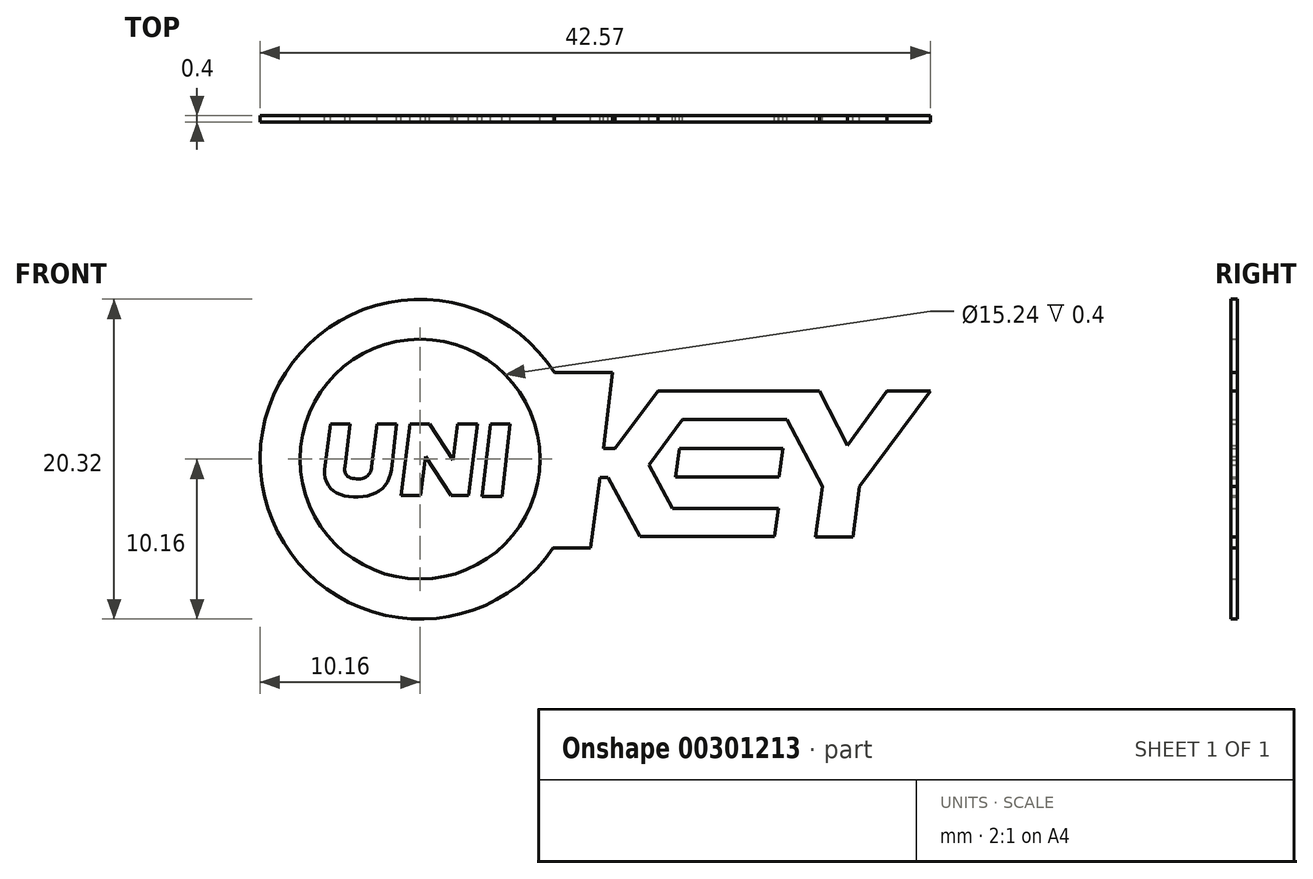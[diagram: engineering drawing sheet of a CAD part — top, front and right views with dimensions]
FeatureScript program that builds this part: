
annotation { "Feature Type Name" : "Feature", "Feature Type Description" : "" }
export const myFeature = defineFeature(function(context is Context, id is Id, definition is map)
    precondition{}
    {
        {
            var Q0;
            Q0=qCreatedBy(makeId("Front.planeOp"),FACE);
            var sketch = newSketch(context, id + "F0", { "sketchPlane" : qUnion([Q0])});
            skSolve(sketch);
        }
        {
            var Q0;
            Q0=qCreatedBy(makeId("Front.planeOp"),FACE);
            var sketch = newSketch(context, id + "F1", { "sketchPlane" : qUnion([Q0])});
            skLineSegment(sketch, "E0.0", {"start": v(106.6, 50.8) * mm, "end": v(0, 50.8) * mm});
            skPoint(sketch, "E1.0", {"position": v(0, 25.4) * mm});
            skLineSegment(sketch, "E2.0", {"start": v(0, 0) * mm, "end": v(106.6, 0) * mm});
            skCircle(sketch, "E3", {"center": v(25.4, 25.4) * mm, "radius": 25.4 * mm});
            skPoint(sketch, "E3.second.point", {"position": v(25.4, 50.8) * mm});
            skPoint(sketch, "E3.third.point", {"position": v(25.4, 0) * mm});
            skCircle(sketch, "E4", {"center": v(25.4, 25.4) * mm, "radius": 19.05 * mm});
            skLineSegment(sketch, "E5", {"start": v(46.75, 39.16) * mm, "end": v(55.96, 39.16) * mm});
            skLineSegment(sketch, "E6", {"start": v(55.96, 39.16) * mm, "end": v(54.52, 27.13) * mm});
            skLineSegment(sketch, "E7", {"start": v(63.19, 36.2) * mm, "end": v(88.82, 36.2) * mm});
            skLineSegment(sketch, "E8", {"start": v(88.82, 36.2) * mm, "end": v(93.23, 27.6) * mm});
            skLineSegment(sketch, "E9", {"start": v(93.23, 27.6) * mm, "end": v(99.5, 36.2) * mm});
            skLineSegment(sketch, "E10", {"start": v(99.5, 36.2) * mm, "end": v(106.42, 36.2) * mm});
            skLineSegment(sketch, "E11", {"start": v(106.42, 36.2) * mm, "end": v(95.19, 21.06) * mm});
            skLineSegment(sketch, "E12", {"start": v(95.19, 21.06) * mm, "end": v(94.13, 13.05) * mm});
            skLineSegment(sketch, "E13", {"start": v(94.13, 13.05) * mm, "end": v(88.2, 13.05) * mm});
            skLineSegment(sketch, "E14", {"start": v(88.2, 13.05) * mm, "end": v(89.26, 21.06) * mm});
            skLineSegment(sketch, "E15", {"start": v(89.26, 21.06) * mm, "end": v(83.67, 31.67) * mm});
            skLineSegment(sketch, "E16", {"start": v(83.67, 31.67) * mm, "end": v(67.1, 31.67) * mm});
            skLineSegment(sketch, "E17", {"start": v(67.1, 31.67) * mm, "end": v(61.78, 24.5) * mm});
            skLineSegment(sketch, "E18", {"start": v(61.78, 24.5) * mm, "end": v(65.5, 17.57) * mm});
            skLineSegment(sketch, "E19", {"start": v(65.5, 17.57) * mm, "end": v(82.3, 17.57) * mm});
            skLineSegment(sketch, "E20", {"start": v(82.3, 17.57) * mm, "end": v(81.7, 13.1) * mm});
            skLineSegment(sketch, "E21", {"start": v(81.7, 13.1) * mm, "end": v(60.3, 13.1) * mm});
            skLineSegment(sketch, "E22", {"start": v(60.3, 13.1) * mm, "end": v(55.26, 22.53) * mm});
            skLineSegment(sketch, "E23", {"start": v(55.26, 22.53) * mm, "end": v(54, 22.53) * mm});
            skLineSegment(sketch, "E24", {"start": v(54, 22.53) * mm, "end": v(52.49, 11.28) * mm});
            skLineSegment(sketch, "E25", {"start": v(52.49, 11.28) * mm, "end": v(46.51, 11.28) * mm});
            skLineSegment(sketch, "E26", {"start": v(54.52, 27.13) * mm, "end": v(56.38, 27.13) * mm});
            skLineSegment(sketch, "E27", {"start": v(56.38, 27.13) * mm, "end": v(63.19, 36.2) * mm});
            skLineSegment(sketch, "E28", {"start": v(66.55, 27.08) * mm, "end": v(65.96, 22.6) * mm});
            skLineSegment(sketch, "E29", {"start": v(65.96, 22.6) * mm, "end": v(82.4, 22.6) * mm});
            skLineSegment(sketch, "E30", {"start": v(82.4, 22.6) * mm, "end": v(83, 27.08) * mm});
            skLineSegment(sketch, "E31", {"start": v(83, 27.08) * mm, "end": v(66.55, 27.08) * mm});
            skLineSegment(sketch, "E32", {"start": v(22.39, 19.63) * mm, "end": v(23.8, 30.97) * mm});
            skLineSegment(sketch, "E33", {"start": v(23.8, 30.97) * mm, "end": v(26.91, 30.97) * mm});
            skLineSegment(sketch, "E34", {"start": v(26.91, 30.97) * mm, "end": v(30.62, 25.3) * mm});
            skLineSegment(sketch, "E35", {"start": v(30.62, 25.3) * mm, "end": v(31.33, 30.97) * mm});
            skLineSegment(sketch, "E36", {"start": v(31.33, 30.97) * mm, "end": v(34.51, 30.97) * mm});
            skLineSegment(sketch, "E37", {"start": v(34.51, 30.97) * mm, "end": v(33.1, 19.63) * mm});
            skLineSegment(sketch, "E38", {"start": v(33.1, 19.63) * mm, "end": v(30.35, 19.63) * mm});
            skLineSegment(sketch, "E39", {"start": v(30.35, 19.63) * mm, "end": v(26.28, 25.87) * mm});
            skLineSegment(sketch, "E40", {"start": v(26.28, 25.87) * mm, "end": v(25.5, 19.63) * mm});
            skLineSegment(sketch, "E41", {"start": v(25.5, 19.63) * mm, "end": v(22.39, 19.63) * mm});
            skLineSegment(sketch, "E42", {"start": v(36.55, 30.97) * mm, "end": v(39.7, 30.97) * mm});
            skLineSegment(sketch, "E43", {"start": v(39.7, 30.97) * mm, "end": v(38.4, 19.49) * mm});
            skLineSegment(sketch, "E44", {"start": v(38.4, 19.49) * mm, "end": v(35.26, 19.49) * mm});
            skLineSegment(sketch, "E45", {"start": v(35.26, 19.49) * mm, "end": v(36.55, 30.97) * mm});
            skLineSegment(sketch, "E46", {"start": v(21.69, 30.97) * mm, "end": v(18.58, 30.97) * mm});
            skLineSegment(sketch, "E47", {"start": v(14.3, 30.97) * mm, "end": v(11.17, 30.97) * mm});
            skLineSegment(sketch, "E48", {"start": v(11.17, 30.97) * mm, "end": v(10.27, 23.75) * mm});
            skLineSegment(sketch, "E49", {"start": v(21.69, 30.97) * mm, "end": v(20.83, 23.75) * mm});
            skFitSpline(sketch, "E50", {"points": [v(10.27, 23.75) * mm, v(10.99, 21) * mm, v(13.2, 19.64) * mm, v(16.86, 19.56) * mm, v(19.54, 20.86) * mm, v(20.83, 23.75) * mm], "startDerivative": vector(-1.98, -15.87) * mm, "endDerivative": vector(1.96, 16.5) * mm});
            skLineSegment(sketch, "E51", {"start": v(14.3, 30.97) * mm, "end": v(13.46, 24.23) * mm});
            skLineSegment(sketch, "E52", {"start": v(18.58, 30.97) * mm, "end": v(17.74, 24.23) * mm});
            skFitSpline(sketch, "E53", {"points": [v(13.46, 24.23) * mm, v(13.64, 22.94) * mm, v(14.65, 22.37) * mm, v(16.2, 22.34) * mm, v(17.33, 23.05) * mm, v(17.74, 24.23) * mm], "startDerivative": vector(-0.9, -7.25) * mm, "endDerivative": vector(0.83, 6.63) * mm});
            skSolve(sketch);
        }
        {
            var Q0;
            Q0=makeQuery(id+"F1.imprint","IMPRINT",FACE,{"disambiguationData":[TD([[makeQuery(id+"F1.imprint","IMPRINT",EDGE,{"derivedFrom":sQuery(id+"F1.wireOp",EDGE,"E28")}),1.0]])]});
            var Q1;
            {var subQ1=sQuery(id+"F1.wireOp",EDGE,"E5");Q1=makeQuery(id+"F1.imprint","IMPRINT",FACE,{"disambiguationData":[TD([[makeQuery(id+"F1.imprint","IMPRINT",EDGE,{"derivedFrom":subQ1}),-1.0]])]});}
            var Q2;
            Q2=makeQuery(id+"F1.imprint","IMPRINT",FACE,{"disambiguationData":[TD([[makeQuery(id+"F1.imprint","IMPRINT",EDGE,{"derivedFrom":sQuery(id+"F1.wireOp",EDGE,"E4")}),-1.0]])]});
            var Q3;
            Q3=makeQuery(id+"F1.imprint","IMPRINT",FACE,{"disambiguationData":[TD([[makeQuery(id+"F1.imprint","IMPRINT",EDGE,{"derivedFrom":sQuery(id+"F1.wireOp",EDGE,"E32")}),-1.0]])]});
            var Q4;
            Q4=makeQuery(id+"F1.imprint","IMPRINT",FACE,{"disambiguationData":[TD([[makeQuery(id+"F1.imprint","IMPRINT",EDGE,{"derivedFrom":sQuery(id+"F1.wireOp",EDGE,"E46")}),1.0]])]});
            var Q5;
            Q5=makeQuery(id+"F1.imprint","IMPRINT",FACE,{"disambiguationData":[TD([[makeQuery(id+"F1.imprint","IMPRINT",EDGE,{"derivedFrom":sQuery(id+"F1.wireOp",EDGE,"E42")}),-1.0]])]});
            extrude(context, id + "F2", {"entities" : qUnion([Q0, Q1, Q2, Q3, Q4, Q5]), "depth" : 1 * mm});
        }
        {
            var Q0;
            Q0=makeQuery(id+"F2.opExtrude","SWEPT_BODY",BODY,{"disambiguationData":[OSD([sQuery(id+"F1.wireOp",EDGE,"E46"),sQuery(id+"F1.wireOp",EDGE,"E47"),sQuery(id+"F1.wireOp",EDGE,"E48"),sQuery(id+"F1.wireOp",EDGE,"E49"),sQuery(id+"F1.wireOp",EDGE,"E50"),sQuery(id+"F1.wireOp",EDGE,"E51"),sQuery(id+"F1.wireOp",EDGE,"E52"),sQuery(id+"F1.wireOp",EDGE,"E53")])]});
            var Q1;
            Q1=makeQuery(id+"F2.opExtrude","SWEPT_BODY",BODY,{"disambiguationData":[OSD([sQuery(id+"F1.wireOp",EDGE,"E42"),sQuery(id+"F1.wireOp",EDGE,"E43"),sQuery(id+"F1.wireOp",EDGE,"E44"),sQuery(id+"F1.wireOp",EDGE,"E45")])]});
            var Q2;
            Q2=makeQuery(id+"F2.opExtrude","SWEPT_BODY",BODY,{"disambiguationData":[OSD([sQuery(id+"F1.wireOp",EDGE,"E32"),sQuery(id+"F1.wireOp",EDGE,"E33"),sQuery(id+"F1.wireOp",EDGE,"E34"),sQuery(id+"F1.wireOp",EDGE,"E35"),sQuery(id+"F1.wireOp",EDGE,"E36"),sQuery(id+"F1.wireOp",EDGE,"E37"),sQuery(id+"F1.wireOp",EDGE,"E38"),sQuery(id+"F1.wireOp",EDGE,"E39"),sQuery(id+"F1.wireOp",EDGE,"E40"),sQuery(id+"F1.wireOp",EDGE,"E41")])]});
            var Q3;
            Q3=makeQuery(id+"F2.opExtrude","SWEPT_BODY",BODY,{"disambiguationData":[OSD([sQuery(id+"F1.wireOp",EDGE,"E28"),sQuery(id+"F1.wireOp",EDGE,"E29"),sQuery(id+"F1.wireOp",EDGE,"E30"),sQuery(id+"F1.wireOp",EDGE,"E31")])]});
            var Q4;
            Q4=makeQuery(id+"F2.opExtrude","SWEPT_BODY",BODY,{"disambiguationData":[OSD([sQuery(id+"F1.wireOp",EDGE,"E3"),sQuery(id+"F1.wireOp",EDGE,"E4"),sQuery(id+"F1.wireOp",EDGE,"E5"),sQuery(id+"F1.wireOp",EDGE,"E6"),sQuery(id+"F1.wireOp",EDGE,"E7"),sQuery(id+"F1.wireOp",EDGE,"E8"),sQuery(id+"F1.wireOp",EDGE,"E9"),sQuery(id+"F1.wireOp",EDGE,"E10"),sQuery(id+"F1.wireOp",EDGE,"E11"),sQuery(id+"F1.wireOp",EDGE,"E12"),sQuery(id+"F1.wireOp",EDGE,"E13"),sQuery(id+"F1.wireOp",EDGE,"E14"),sQuery(id+"F1.wireOp",EDGE,"E15"),sQuery(id+"F1.wireOp",EDGE,"E16"),sQuery(id+"F1.wireOp",EDGE,"E17"),sQuery(id+"F1.wireOp",EDGE,"E18"),sQuery(id+"F1.wireOp",EDGE,"E19"),sQuery(id+"F1.wireOp",EDGE,"E20"),sQuery(id+"F1.wireOp",EDGE,"E21"),sQuery(id+"F1.wireOp",EDGE,"E22"),sQuery(id+"F1.wireOp",EDGE,"E23"),sQuery(id+"F1.wireOp",EDGE,"E24"),sQuery(id+"F1.wireOp",EDGE,"E25"),sQuery(id+"F1.wireOp",EDGE,"E26"),sQuery(id+"F1.wireOp",EDGE,"E27")])]});
            var Q5;
            Q5=qCreatedBy(makeId("Origin.pointOp"),VERTEX);
            transform(context, id + "F3", {"entities" : qUnion([Q0, Q1, Q2, Q3, Q4]), "transformType" : TransformType.SCALE_UNIFORMLY, "scale" : .4, "scalePoint" : qUnion([Q5]), "makeCopy" : false});
        }
    });
